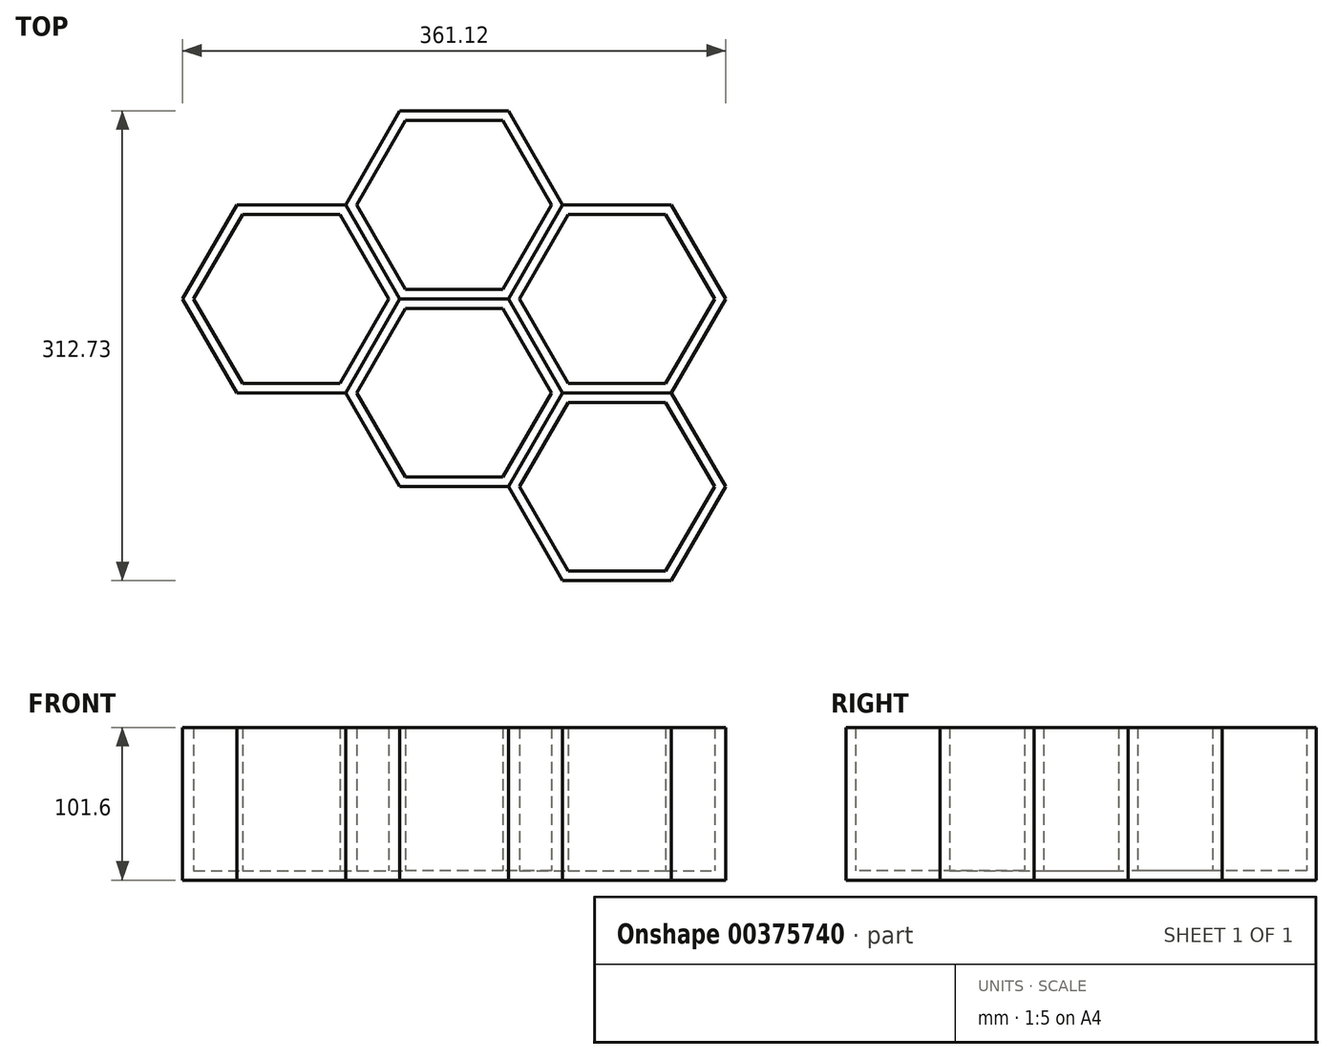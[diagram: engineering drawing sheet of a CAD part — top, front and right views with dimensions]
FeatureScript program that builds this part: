
annotation { "Feature Type Name" : "Feature", "Feature Type Description" : "" }
export const myFeature = defineFeature(function(context is Context, id is Id, definition is map)
    precondition{}
    {
        {
            var Q0;
            Q0=qCreatedBy(makeId("Top.planeOp"),FACE);
            var sketch = newSketch(context, id + "F0", { "sketchPlane" : qUnion([Q0])});
            skCircle(sketch, "E0.cCircle", {"center": v(0, 0) * mm, "radius": 62.55 * mm, "construction": true});
            skLineSegment(sketch, "E0.0", {"start": v(36.11, -62.55) * mm, "end": v(-36.11, -62.55) * mm});
            skLineSegment(sketch, "E0.1", {"start": v(-36.11, -62.55) * mm, "end": v(-72.22, 0) * mm});
            skLineSegment(sketch, "E0.2", {"start": v(-72.22, 0) * mm, "end": v(-36.11, 62.55) * mm});
            skLineSegment(sketch, "E0.3", {"start": v(-36.11, 62.55) * mm, "end": v(36.11, 62.55) * mm});
            skLineSegment(sketch, "E0.4", {"start": v(36.11, 62.55) * mm, "end": v(72.22, 0) * mm});
            skLineSegment(sketch, "E0.5", {"start": v(72.22, 0) * mm, "end": v(36.11, -62.55) * mm});
            skPoint(sketch, "E0.0.midPoint", {"position": v(0, -62.55) * mm});
            skSolve(sketch);
        }
        {
            var Q0;
            Q0 = qSketchRegion(id + "F0", true);
            extrude(context, id + "F1", {"entities" : qUnion([Q0]), "depth" : 101.6 * mm});
        }
        {
            var Q0;
            Q0=makeQuery(id+"F1.opExtrude","CAP_FACE",FACE,{"disambiguationData":[OSD([sQuery(id+"F0.wireOp",EDGE,"E0.0"),sQuery(id+"F0.wireOp",EDGE,"E0.1"),sQuery(id+"F0.wireOp",EDGE,"E0.2"),sQuery(id+"F0.wireOp",EDGE,"E0.3"),sQuery(id+"F0.wireOp",EDGE,"E0.4"),sQuery(id+"F0.wireOp",EDGE,"E0.5")])],"isStart":false});
            shell(context, id + "F2", {"entities" : qUnion([Q0]), "thickness" : 6.35 * mm});
        }
        {
            var Q0;
            Q0=makeQuery(id+"F1.opExtrude","SWEPT_BODY",BODY,{"disambiguationData":[OSD([sQuery(id+"F0.wireOp",EDGE,"E0.0"),sQuery(id+"F0.wireOp",EDGE,"E0.1"),sQuery(id+"F0.wireOp",EDGE,"E0.2"),sQuery(id+"F0.wireOp",EDGE,"E0.3"),sQuery(id+"F0.wireOp",EDGE,"E0.4"),sQuery(id+"F0.wireOp",EDGE,"E0.5")])]});
            var Q1;
            Q1=makeQuery(id+"F1.opExtrude","SWEPT_EDGE",EDGE,{"disambiguationData":[OSD([sQuery(id+"F0.wireOp",EDGE,"E0.0"),sQuery(id+"F0.wireOp",EDGE,"E0.1")])]});
            circularPattern(context, id + "F3", {"entities" : qUnion([Q0]), "axis" : qUnion([Q1]), "angle" : 360 * degree, "instanceCount" : 3, "equalSpace" : true});
        }
        {
            var Q0;
            Q0=makeQuery(id+"F3.opPattern","COPY",BODY,{"derivedFrom":makeQuery(id+"F1.opExtrude","SWEPT_BODY",BODY,{"disambiguationData":[OSD([sQuery(id+"F0.wireOp",EDGE,"E0.0"),sQuery(id+"F0.wireOp",EDGE,"E0.1"),sQuery(id+"F0.wireOp",EDGE,"E0.2"),sQuery(id+"F0.wireOp",EDGE,"E0.3"),sQuery(id+"F0.wireOp",EDGE,"E0.4"),sQuery(id+"F0.wireOp",EDGE,"E0.5")])]}),"instanceName":"1"});
            var Q1;
            Q1=makeQuery(id+"F3.opPattern","COPY",EDGE,{"derivedFrom":makeQuery(id+"F1.opExtrude","SWEPT_EDGE",EDGE,{"disambiguationData":[OSD([sQuery(id+"F0.wireOp",EDGE,"E0.2"),sQuery(id+"F0.wireOp",EDGE,"E0.3")])]}),"instanceName":"1"});
            circularPattern(context, id + "F4", {"entities" : qUnion([Q0]), "axis" : qUnion([Q1]), "angle" : 360 * degree, "instanceCount" : 3, "equalSpace" : true});
        }
    });
